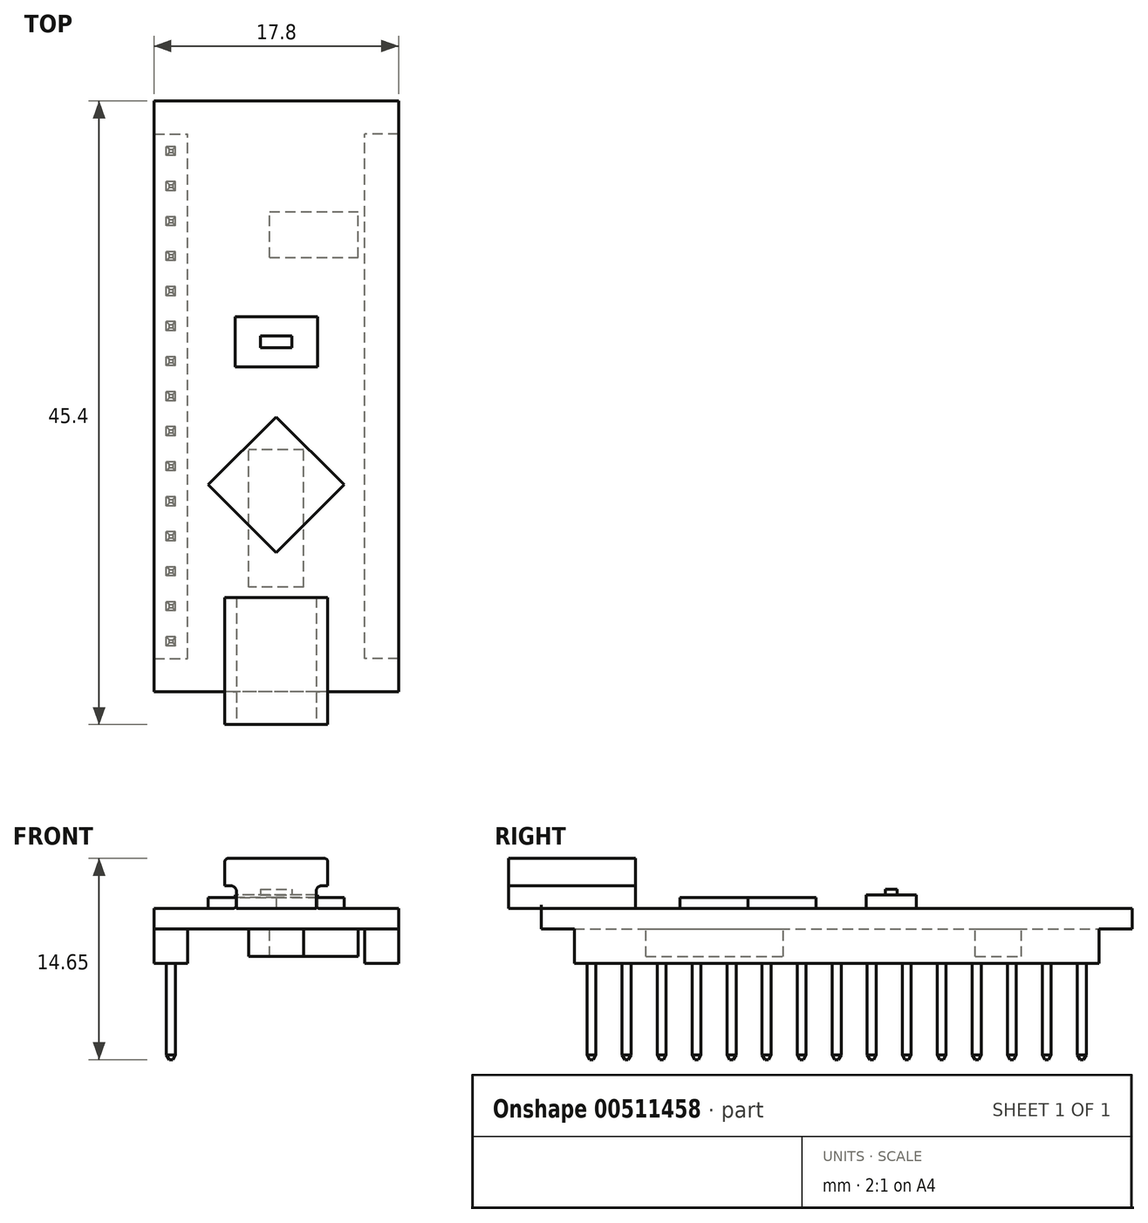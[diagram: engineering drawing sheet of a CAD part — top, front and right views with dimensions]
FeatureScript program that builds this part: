
annotation { "Feature Type Name" : "Feature", "Feature Type Description" : "" }
export const myFeature = defineFeature(function(context is Context, id is Id, definition is map)
    precondition{}
    {
        {
            var Q0;
            Q0=qCreatedBy(makeId("Top.planeOp"),FACE);
            var sketch = newSketch(context, id + "F0", { "sketchPlane" : qUnion([Q0])});
            skLineSegment(sketch, "E0.bottom", {"start": v(8.9, 21.5) * mm, "end": v(-8.9, 21.5) * mm});
            skLineSegment(sketch, "E0.top", {"start": v(8.9, -21.5) * mm, "end": v(-8.9, -21.5) * mm});
            skLineSegment(sketch, "E0.left", {"start": v(8.9, 21.5) * mm, "end": v(8.9, -21.5) * mm});
            skLineSegment(sketch, "E0.right", {"start": v(-8.9, 21.5) * mm, "end": v(-8.9, -21.5) * mm});
            skPoint(sketch, "E0.middle", {"position": v(0, 0) * mm});
            skSolve(sketch);
        }
        {
            var Q0;
            Q0=qSketchRegion(id+"F0",true);
            extrude(context, id + "F1", {"entities" : qUnion([Q0]), "depth" : 1.5 * mm, "offsetDistance" : 25 * mm});
        }
        {
            var Q0;
            Q0=makeQuery(id+"F1.opExtrude","CAP_FACE",FACE,{"disambiguationData":[OSD([sQuery(id+"F0.wireOp",EDGE,"E0.bottom"),sQuery(id+"F0.wireOp",EDGE,"E0.top"),sQuery(id+"F0.wireOp",EDGE,"E0.left"),sQuery(id+"F0.wireOp",EDGE,"E0.right")])],"isStart":false});
            var sketch = newSketch(context, id + "F2", { "sketchPlane" : qUnion([Q0])});
            skLineSegment(sketch, "E1", {"start": v(0, -1.5) * mm, "end": v(4.95, -6.45) * mm});
            skLineSegment(sketch, "E2", {"start": v(4.95, -6.45) * mm, "end": v(0, -11.4) * mm});
            skLineSegment(sketch, "E3", {"start": v(0, -11.4) * mm, "end": v(-4.95, -6.45) * mm});
            skLineSegment(sketch, "E4", {"start": v(-4.95, -6.45) * mm, "end": v(0, -1.5) * mm});
            skSolve(sketch);
        }
        {
            var Q0;
            Q0=qSketchRegion(id+"F2",true);
            extrude(context, id + "F3", {"entities" : qUnion([Q0]), "operationType" : NewBodyOperationType.ADD, "depth" : 0.8 * mm, "offsetDistance" : 25 * mm});
        }
        {
            var Q0;
            Q0=makeQuery(id+"F1.opExtrude","CAP_FACE",FACE,{"disambiguationData":[OSD([sQuery(id+"F0.wireOp",EDGE,"E0.bottom"),sQuery(id+"F0.wireOp",EDGE,"E0.top"),sQuery(id+"F0.wireOp",EDGE,"E0.left"),sQuery(id+"F0.wireOp",EDGE,"E0.right")])],"isStart":false});
            var sketch = newSketch(context, id + "F4", { "sketchPlane" : qUnion([Q0])});
            skLineSegment(sketch, "E5.bottom", {"start": v(3, 5.8) * mm, "end": v(-3, 5.8) * mm});
            skLineSegment(sketch, "E5.top", {"start": v(3, 2.15) * mm, "end": v(-3, 2.15) * mm});
            skLineSegment(sketch, "E5.left", {"start": v(3, 5.8) * mm, "end": v(3, 2.15) * mm});
            skLineSegment(sketch, "E5.right", {"start": v(-3, 5.8) * mm, "end": v(-3, 2.15) * mm});
            skPoint(sketch, "E5.middle", {"position": v(0, 3.98) * mm});
            skSolve(sketch);
        }
        {
            var Q0;
            Q0=qSketchRegion(id+"F4",true);
            extrude(context, id + "F5", {"entities" : qUnion([Q0]), "operationType" : NewBodyOperationType.ADD, "depth" : 1 * mm, "offsetDistance" : 25 * mm});
        }
        {
            var Q0;
            Q0=makeQuery(id+"F5.opExtrude","CAP_FACE",FACE,{"disambiguationData":[OSD([sQuery(id+"F4.wireOp",EDGE,"E5.bottom"),sQuery(id+"F4.wireOp",EDGE,"E5.top"),sQuery(id+"F4.wireOp",EDGE,"E5.left"),sQuery(id+"F4.wireOp",EDGE,"E5.right")])],"isStart":false});
            var sketch = newSketch(context, id + "F6", { "sketchPlane" : qUnion([Q0])});
            skLineSegment(sketch, "E6.bottom", {"start": v(-1.15, 4.4) * mm, "end": v(1.15, 4.4) * mm});
            skLineSegment(sketch, "E6.top", {"start": v(-1.15, 3.55) * mm, "end": v(1.15, 3.55) * mm});
            skLineSegment(sketch, "E6.left", {"start": v(-1.15, 4.4) * mm, "end": v(-1.15, 3.55) * mm});
            skLineSegment(sketch, "E6.right", {"start": v(1.15, 4.4) * mm, "end": v(1.15, 3.55) * mm});
            skPoint(sketch, "E6.middle", {"position": v(0, 3.98) * mm});
            skPoint(sketch, "E6.middle.positionSnap0", {"position": v(-3, 3.98) * mm});
            skPoint(sketch, "E6.middle.positionSnap1", {"position": v(0, 5.8) * mm});
            skPoint(sketch, "E6.centerSnap0", {"position": v(-3, 3.98) * mm});
            skPoint(sketch, "E6.centerSnap1", {"position": v(0, 5.8) * mm});
            skSolve(sketch);
        }
        {
            var Q0;
            Q0=qSketchRegion(id+"F6",true);
            extrude(context, id + "F7", {"entities" : qUnion([Q0]), "operationType" : NewBodyOperationType.ADD, "depth" : 0.4 * mm, "offsetDistance" : 25 * mm});
        }
        {
            var Q0;
            Q0=makeQuery(id+"F1.opExtrude","CAP_FACE",FACE,{"disambiguationData":[OSD([sQuery(id+"F0.wireOp",EDGE,"E0.bottom"),sQuery(id+"F0.wireOp",EDGE,"E0.top"),sQuery(id+"F0.wireOp",EDGE,"E0.left"),sQuery(id+"F0.wireOp",EDGE,"E0.right")])],"isStart":false});
            var sketch = newSketch(context, id + "F8", { "sketchPlane" : qUnion([Q0])});
            skLineSegment(sketch, "E7.bottom", {"start": v(3.75, -19.1) * mm, "end": v(-3.75, -19.1) * mm});
            skLineSegment(sketch, "E7.top", {"start": v(3.75, -23.9) * mm, "end": v(-3.75, -23.9) * mm});
            skLineSegment(sketch, "E7.left", {"start": v(3.75, -19.1) * mm, "end": v(3.75, -23.9) * mm});
            skLineSegment(sketch, "E7.right", {"start": v(-3.75, -19.1) * mm, "end": v(-3.75, -23.9) * mm});
            skPoint(sketch, "E7.middle", {"position": v(0, -21.5) * mm});
            skLineSegment(sketch, "E8.bottom", {"start": v(-3.75, -19.1) * mm, "end": v(3.75, -19.1) * mm});
            skLineSegment(sketch, "E8.top", {"start": v(-3.75, -14.65) * mm, "end": v(3.75, -14.65) * mm});
            skLineSegment(sketch, "E8.left", {"start": v(-3.75, -19.1) * mm, "end": v(-3.75, -14.65) * mm});
            skLineSegment(sketch, "E8.right", {"start": v(3.75, -19.1) * mm, "end": v(3.75, -14.65) * mm});
            skSolve(sketch);
        }
        {
            var Q0;
            Q0=qSketchRegion(id+"F8",true);
            extrude(context, id + "F9", {"entities" : qUnion([Q0]), "operationType" : NewBodyOperationType.ADD, "depth" : 3.65 * mm, "offsetDistance" : 25 * mm});
        }
        {
            var Q0;
            Q0=makeQuery(id+"F9.opExtrude","SWEPT_FACE",FACE,{"disambiguationData":[OSD([sQuery(id+"F8.wireOp",EDGE,"E7.top")])]});
            var sketch = newSketch(context, id + "F10", { "sketchPlane" : qUnion([Q0])});
            skLineSegment(sketch, "E9.bottom", {"start": v(-3.75, 3.15) * mm, "end": v(-2.9, 3.15) * mm});
            skLineSegment(sketch, "E9.top", {"start": v(-3.75, 1.5) * mm, "end": v(-2.9, 1.5) * mm});
            skLineSegment(sketch, "E9.left", {"start": v(-3.75, 3.15) * mm, "end": v(-3.75, 1.5) * mm});
            skLineSegment(sketch, "E9.right", {"start": v(-2.9, 3.15) * mm, "end": v(-2.9, 1.5) * mm});
            skLineSegment(sketch, "E10.bottom", {"start": v(3.75, 3.15) * mm, "end": v(2.9, 3.15) * mm});
            skLineSegment(sketch, "E10.top", {"start": v(3.75, 1.5) * mm, "end": v(2.9, 1.5) * mm});
            skLineSegment(sketch, "E10.left", {"start": v(3.75, 3.15) * mm, "end": v(3.75, 1.5) * mm});
            skLineSegment(sketch, "E10.right", {"start": v(2.9, 3.15) * mm, "end": v(2.9, 1.5) * mm});
            skSolve(sketch);
        }
        {
            var Q0;
            Q0=qSketchRegion(id+"F10",true);
            var Q1;
            Q1=makeQuery(id+"F9.opExtrude","SWEPT_FACE",FACE,{"disambiguationData":[OSD([sQuery(id+"F8.wireOp",EDGE,"E8.top")])]});
            extrude(context, id + "F11", {"entities" : qUnion([Q0]), "operationType" : NewBodyOperationType.REMOVE, "endBound" : BoundingType.UP_TO_SURFACE, "oppositeDirection" : true, "depth" : 25 * mm, "endBoundEntityFace" : qUnion([Q1]), "offsetDistance" : 25 * mm});
        }
        {
            var Q0;
            Q0=makeQuery(id+"F11.boolean.opBoolean","COPY",EDGE,{"derivedFrom":makeQuery(id+"F11.opExtrude","SWEPT_EDGE",EDGE,{"disambiguationData":[OSD([sQuery(id+"F10.wireOp",EDGE,"E9.bottom"),sQuery(id+"F10.wireOp",EDGE,"E9.right")])]})});
            var Q1;
            Q1=makeQuery(id+"F11.boolean.opBoolean","COPY",EDGE,{"derivedFrom":makeQuery(id+"F11.opExtrude","SWEPT_EDGE",EDGE,{"disambiguationData":[OSD([sQuery(id+"F8.wireOp",EDGE,"E7.top"),sQuery(id+"F8.wireOp",EDGE,"E7.right"),sQuery(id+"F10.wireOp",EDGE,"E9.bottom"),sQuery(id+"F10.wireOp",EDGE,"E9.left")])]})});
            var Q2;
            Q2=makeQuery(id+"F11.boolean.opBoolean","COPY",EDGE,{"derivedFrom":makeQuery(id+"F11.opExtrude","SWEPT_EDGE",EDGE,{"disambiguationData":[OSD([sQuery(id+"F10.wireOp",EDGE,"E10.bottom"),sQuery(id+"F10.wireOp",EDGE,"E10.right")])]})});
            var Q3;
            Q3=makeQuery(id+"F11.boolean.opBoolean","COPY",EDGE,{"derivedFrom":makeQuery(id+"F11.opExtrude","SWEPT_EDGE",EDGE,{"disambiguationData":[OSD([sQuery(id+"F8.wireOp",EDGE,"E7.top"),sQuery(id+"F8.wireOp",EDGE,"E7.left"),sQuery(id+"F10.wireOp",EDGE,"E10.bottom"),sQuery(id+"F10.wireOp",EDGE,"E10.left")])]})});
            fillet(context, id + "F12", {"entities" : qUnion([Q0, Q1, Q2, Q3]), "radius" : 0.4 * mm, "tangentPropagation" : true, "allowEdgeOverflow" : false});
        }
        {
            var Q0;
            Q0=makeQuery(id+"F9.opExtrude","CAP_EDGE",EDGE,{"disambiguationData":[OSD([sQuery(id+"F8.wireOp",EDGE,"E7.right"),sQuery(id+"F8.wireOp",EDGE,"E8.left")])],"isStart":false});
            var Q1;
            Q1=makeQuery(id+"F9.opExtrude","CAP_EDGE",EDGE,{"disambiguationData":[OSD([sQuery(id+"F8.wireOp",EDGE,"E7.left"),sQuery(id+"F8.wireOp",EDGE,"E8.right")])],"isStart":false});
            var Q2;
            {var subQ0=sQuery(id+"F8.wireOp",EDGE,"E7.top");var subQ1=sQuery(id+"F10.wireOp",EDGE,"E9.right");Q2=makeQuery(id+"F11.boolean.opBoolean","COPY",EDGE,{"disambiguationData":[topologyDisambiguationEdgeConnected([makeQuery(id+"F9.opExtrude","CAP_FACE",FACE,{"disambiguationData":[OSD([subQ0,sQuery(id+"F8.wireOp",EDGE,"E7.left"),sQuery(id+"F8.wireOp",EDGE,"E7.right"),sQuery(id+"F8.wireOp",EDGE,"E8.top"),sQuery(id+"F8.wireOp",EDGE,"E8.left"),sQuery(id+"F8.wireOp",EDGE,"E8.right")])],"isStart":true})])],"derivedFrom":makeQuery(id+"F11.opExtrude","SWEPT_EDGE",EDGE,{"disambiguationData":[OSD([subQ0,sQuery(id+"F10.wireOp",EDGE,"E9.top"),subQ1])]})});}
            var Q3;
            {var subQ0=sQuery(id+"F8.wireOp",EDGE,"E7.top");var subQ1=sQuery(id+"F10.wireOp",EDGE,"E10.right");Q3=makeQuery(id+"F11.boolean.opBoolean","COPY",EDGE,{"disambiguationData":[topologyDisambiguationEdgeConnected([makeQuery(id+"F9.opExtrude","CAP_FACE",FACE,{"disambiguationData":[OSD([subQ0,sQuery(id+"F8.wireOp",EDGE,"E7.left"),sQuery(id+"F8.wireOp",EDGE,"E7.right"),sQuery(id+"F8.wireOp",EDGE,"E8.top"),sQuery(id+"F8.wireOp",EDGE,"E8.left"),sQuery(id+"F8.wireOp",EDGE,"E8.right")])],"isStart":true})])],"derivedFrom":makeQuery(id+"F11.opExtrude","SWEPT_EDGE",EDGE,{"disambiguationData":[OSD([subQ0,sQuery(id+"F10.wireOp",EDGE,"E10.top"),subQ1])]})});}
            fillet(context, id + "F13", {"entities" : qUnion([Q0, Q1, Q2, Q3]), "radius" : 0.25 * mm, "tangentPropagation" : true, "allowEdgeOverflow" : false});
        }
        {
            var Q0;
            Q0=makeQuery(id+"F1.opExtrude","CAP_FACE",FACE,{"disambiguationData":[OSD([sQuery(id+"F0.wireOp",EDGE,"E0.bottom"),sQuery(id+"F0.wireOp",EDGE,"E0.top"),sQuery(id+"F0.wireOp",EDGE,"E0.left"),sQuery(id+"F0.wireOp",EDGE,"E0.right")])],"isStart":true});
            var sketch = newSketch(context, id + "F14", { "sketchPlane" : qUnion([Q0])});
            skLineSegment(sketch, "E11.bottom", {"start": v(-8.9, 19.1) * mm, "end": v(-6.45, 19.1) * mm});
            skLineSegment(sketch, "E11.top", {"start": v(-8.9, -19.1) * mm, "end": v(-6.45, -19.1) * mm});
            skLineSegment(sketch, "E11.left", {"start": v(-8.9, 19.1) * mm, "end": v(-8.9, -19.1) * mm});
            skLineSegment(sketch, "E11.right", {"start": v(-6.45, 19.1) * mm, "end": v(-6.45, -19.1) * mm});
            skLineSegment(sketch, "E12.bottom", {"start": v(8.9, 19.1) * mm, "end": v(6.45, 19.1) * mm});
            skLineSegment(sketch, "E12.top", {"start": v(8.9, -19.1) * mm, "end": v(6.45, -19.1) * mm});
            skLineSegment(sketch, "E12.left", {"start": v(8.9, 19.1) * mm, "end": v(8.9, -19.1) * mm});
            skLineSegment(sketch, "E12.right", {"start": v(6.45, 19.1) * mm, "end": v(6.45, -19.1) * mm});
            skSolve(sketch);
        }
        {
            var Q0;
            Q0=qSketchRegion(id+"F14",true);
            extrude(context, id + "F15", {"entities" : qUnion([Q0]), "operationType" : NewBodyOperationType.ADD, "depth" : 2.5 * mm, "offsetDistance" : 25 * mm});
        }
        {
            var Q0;
            Q0=makeQuery(id+"F15.opExtrude","CAP_FACE",FACE,{"disambiguationData":[OSD([sQuery(id+"F14.wireOp",EDGE,"E11.bottom"),sQuery(id+"F14.wireOp",EDGE,"E11.top"),sQuery(id+"F14.wireOp",EDGE,"E11.left"),sQuery(id+"F14.wireOp",EDGE,"E11.right")])],"isStart":false});
            var sketch = newSketch(context, id + "F16", { "sketchPlane" : qUnion([Q0])});
            skLineSegment(sketch, "E13.bottom", {"start": v(-7.35, 18.18) * mm, "end": v(-8, 18.18) * mm});
            skLineSegment(sketch, "E13.top", {"start": v(-7.35, 17.53) * mm, "end": v(-8, 17.53) * mm});
            skLineSegment(sketch, "E13.left", {"start": v(-7.35, 18.18) * mm, "end": v(-7.35, 17.53) * mm});
            skLineSegment(sketch, "E13.right", {"start": v(-8, 18.18) * mm, "end": v(-8, 17.53) * mm});
            skPoint(sketch, "E13.middle", {"position": v(-7.68, 17.85) * mm});
            skPoint(sketch, "E13.middle.positionSnap0", {"position": v(-7.68, 19.1) * mm});
            skPoint(sketch, "E13.centerSnap0", {"position": v(-7.68, 19.1) * mm});
            skLineSegment(sketch, "E14.0.1.0", {"start": v(-7.35, 15.63) * mm, "end": v(-8, 15.63) * mm});
            skLineSegment(sketch, "E14.0.1.1", {"start": v(-7.35, 15.63) * mm, "end": v(-7.35, 14.98) * mm});
            skLineSegment(sketch, "E14.0.1.2", {"start": v(-8, 15.63) * mm, "end": v(-8, 14.98) * mm});
            skLineSegment(sketch, "E14.0.1.3", {"start": v(-7.35, 14.98) * mm, "end": v(-8, 14.98) * mm});
            skLineSegment(sketch, "E14.0.2.0", {"start": v(-7.35, 13.08) * mm, "end": v(-8, 13.08) * mm});
            skLineSegment(sketch, "E14.0.2.1", {"start": v(-7.35, 13.08) * mm, "end": v(-7.35, 12.43) * mm});
            skLineSegment(sketch, "E14.0.2.2", {"start": v(-8, 13.08) * mm, "end": v(-8, 12.43) * mm});
            skLineSegment(sketch, "E14.0.2.3", {"start": v(-7.35, 12.43) * mm, "end": v(-8, 12.43) * mm});
            skLineSegment(sketch, "E14.0.3.0", {"start": v(-7.35, 10.53) * mm, "end": v(-8, 10.53) * mm});
            skLineSegment(sketch, "E14.0.3.1", {"start": v(-7.35, 10.53) * mm, "end": v(-7.35, 9.88) * mm});
            skLineSegment(sketch, "E14.0.3.2", {"start": v(-8, 10.53) * mm, "end": v(-8, 9.88) * mm});
            skLineSegment(sketch, "E14.0.3.3", {"start": v(-7.35, 9.88) * mm, "end": v(-8, 9.88) * mm});
            skLineSegment(sketch, "E14.0.4.0", {"start": v(-7.35, 7.98) * mm, "end": v(-8, 7.98) * mm});
            skLineSegment(sketch, "E14.0.4.1", {"start": v(-7.35, 7.98) * mm, "end": v(-7.35, 7.33) * mm});
            skLineSegment(sketch, "E14.0.4.2", {"start": v(-8, 7.98) * mm, "end": v(-8, 7.33) * mm});
            skLineSegment(sketch, "E14.0.4.3", {"start": v(-7.35, 7.33) * mm, "end": v(-8, 7.33) * mm});
            skLineSegment(sketch, "E14.0.5.0", {"start": v(-7.35, 5.43) * mm, "end": v(-8, 5.43) * mm});
            skLineSegment(sketch, "E14.0.5.1", {"start": v(-7.35, 5.43) * mm, "end": v(-7.35, 4.78) * mm});
            skLineSegment(sketch, "E14.0.5.2", {"start": v(-8, 5.43) * mm, "end": v(-8, 4.78) * mm});
            skLineSegment(sketch, "E14.0.5.3", {"start": v(-7.35, 4.78) * mm, "end": v(-8, 4.78) * mm});
            skLineSegment(sketch, "E14.0.6.0", {"start": v(-7.35, 2.88) * mm, "end": v(-8, 2.88) * mm});
            skLineSegment(sketch, "E14.0.6.1", {"start": v(-7.35, 2.88) * mm, "end": v(-7.35, 2.23) * mm});
            skLineSegment(sketch, "E14.0.6.2", {"start": v(-8, 2.88) * mm, "end": v(-8, 2.23) * mm});
            skLineSegment(sketch, "E14.0.6.3", {"start": v(-7.35, 2.23) * mm, "end": v(-8, 2.23) * mm});
            skLineSegment(sketch, "E14.0.7.0", {"start": v(-7.35, 0.33) * mm, "end": v(-8, 0.33) * mm});
            skLineSegment(sketch, "E14.0.7.1", {"start": v(-7.35, 0.33) * mm, "end": v(-7.35, -0.32) * mm});
            skLineSegment(sketch, "E14.0.7.2", {"start": v(-8, 0.33) * mm, "end": v(-8, -0.32) * mm});
            skLineSegment(sketch, "E14.0.7.3", {"start": v(-7.35, -0.32) * mm, "end": v(-8, -0.32) * mm});
            skLineSegment(sketch, "E14.0.8.0", {"start": v(-7.35, -2.22) * mm, "end": v(-8, -2.22) * mm});
            skLineSegment(sketch, "E14.0.8.1", {"start": v(-7.35, -2.22) * mm, "end": v(-7.35, -2.87) * mm});
            skLineSegment(sketch, "E14.0.8.2", {"start": v(-8, -2.22) * mm, "end": v(-8, -2.87) * mm});
            skLineSegment(sketch, "E14.0.8.3", {"start": v(-7.35, -2.87) * mm, "end": v(-8, -2.87) * mm});
            skLineSegment(sketch, "E14.0.9.0", {"start": v(-7.35, -4.77) * mm, "end": v(-8, -4.77) * mm});
            skLineSegment(sketch, "E14.0.9.1", {"start": v(-7.35, -4.77) * mm, "end": v(-7.35, -5.42) * mm});
            skLineSegment(sketch, "E14.0.9.2", {"start": v(-8, -4.77) * mm, "end": v(-8, -5.42) * mm});
            skLineSegment(sketch, "E14.0.9.3", {"start": v(-7.35, -5.42) * mm, "end": v(-8, -5.42) * mm});
            skLineSegment(sketch, "E14.0.10.0", {"start": v(-7.35, -7.32) * mm, "end": v(-8, -7.32) * mm});
            skLineSegment(sketch, "E14.0.10.1", {"start": v(-7.35, -7.32) * mm, "end": v(-7.35, -7.97) * mm});
            skLineSegment(sketch, "E14.0.10.2", {"start": v(-8, -7.32) * mm, "end": v(-8, -7.97) * mm});
            skLineSegment(sketch, "E14.0.10.3", {"start": v(-7.35, -7.97) * mm, "end": v(-8, -7.97) * mm});
            skLineSegment(sketch, "E14.0.11.0", {"start": v(-7.35, -9.87) * mm, "end": v(-8, -9.87) * mm});
            skLineSegment(sketch, "E14.0.11.1", {"start": v(-7.35, -9.87) * mm, "end": v(-7.35, -10.52) * mm});
            skLineSegment(sketch, "E14.0.11.2", {"start": v(-8, -9.87) * mm, "end": v(-8, -10.52) * mm});
            skLineSegment(sketch, "E14.0.11.3", {"start": v(-7.35, -10.52) * mm, "end": v(-8, -10.52) * mm});
            skLineSegment(sketch, "E14.0.12.0", {"start": v(-7.35, -12.42) * mm, "end": v(-8, -12.42) * mm});
            skLineSegment(sketch, "E14.0.12.1", {"start": v(-7.35, -12.42) * mm, "end": v(-7.35, -13.07) * mm});
            skLineSegment(sketch, "E14.0.12.2", {"start": v(-8, -12.42) * mm, "end": v(-8, -13.07) * mm});
            skLineSegment(sketch, "E14.0.12.3", {"start": v(-7.35, -13.07) * mm, "end": v(-8, -13.07) * mm});
            skLineSegment(sketch, "E14.0.13.0", {"start": v(-7.35, -14.97) * mm, "end": v(-8, -14.97) * mm});
            skLineSegment(sketch, "E14.0.13.1", {"start": v(-7.35, -14.97) * mm, "end": v(-7.35, -15.62) * mm});
            skLineSegment(sketch, "E14.0.13.2", {"start": v(-8, -14.97) * mm, "end": v(-8, -15.62) * mm});
            skLineSegment(sketch, "E14.0.13.3", {"start": v(-7.35, -15.62) * mm, "end": v(-8, -15.62) * mm});
            skLineSegment(sketch, "E14.0.14.0", {"start": v(-7.35, -17.52) * mm, "end": v(-8, -17.52) * mm});
            skLineSegment(sketch, "E14.0.14.1", {"start": v(-7.35, -17.52) * mm, "end": v(-7.35, -18.17) * mm});
            skLineSegment(sketch, "E14.0.14.2", {"start": v(-8, -17.52) * mm, "end": v(-8, -18.17) * mm});
            skLineSegment(sketch, "E14.0.14.3", {"start": v(-7.35, -18.17) * mm, "end": v(-8, -18.17) * mm});
            skLineSegment(sketch, "E14.direction1", {"start": v(-8, 18.18) * mm, "end": v(17, 18.18) * mm, "construction": true});
            skLineSegment(sketch, "E14.direction2", {"start": v(-8, 18.18) * mm, "end": v(-8, 15.63) * mm, "construction": true});
            skSolve(sketch);
        }
        {
            var Q0;
            Q0=qSketchRegion(id+"F16",true);
            extrude(context, id + "F17", {"entities" : qUnion([Q0]), "operationType" : NewBodyOperationType.ADD, "depth" : 7 * mm, "offsetDistance" : 25 * mm});
        }
        {
            var Q0;
            Q0=makeQuery(id+"F1.opExtrude","CAP_EDGE",EDGE,{"disambiguationData":[OSD([sQuery(id+"F0.wireOp",EDGE,"E0.top")])],"isStart":true});
            cPoint(context, id + "F18", {"entities" : qUnion([Q0]), "parameter" : 0.5});
        }
        {
            var Q0;
            Q0=makeQuery(id+"F1.opExtrude","CAP_EDGE",EDGE,{"disambiguationData":[OSD([sQuery(id+"F0.wireOp",EDGE,"E0.bottom")])],"isStart":true});
            cPoint(context, id + "F19", {"entities" : qUnion([Q0]), "parameter" : 0.5});
        }
        {
            var Q0;
            Q0=makeQuery(id+"F1.opExtrude","CAP_EDGE",EDGE,{"disambiguationData":[OSD([sQuery(id+"F0.wireOp",EDGE,"E0.bottom")])],"isStart":false});
            cPoint(context, id + "F20", {"entities" : qUnion([Q0]), "parameter" : 0.5});
        }
        {
            var Q0;
            Q0=qCreatedBy(id+"F18",VERTEX);
            var Q1;
            Q1=qCreatedBy(id+"F19",VERTEX);
            var Q2;
            Q2=qCreatedBy(id+"F20",VERTEX);
            cPlane(context, id + "F21", {"entities" : qUnion([Q0, Q1, Q2]), "cplaneType" : CPlaneType.THREE_POINT, "offset" : 25 * mm, "width" : 150 * mm, "height" : 150 * mm});
        }
        {
            var Q0;
            Q0=makeQuery(id+"F17.opExtrude","CAP_EDGE",EDGE,{"disambiguationData":[OSD([sQuery(id+"F16.wireOp",EDGE,"E13.right")])],"isStart":false});
            var Q1;
            Q1=makeQuery(id+"F17.opExtrude","CAP_EDGE",EDGE,{"disambiguationData":[OSD([sQuery(id+"F16.wireOp",EDGE,"E13.top")])],"isStart":false});
            var Q2;
            Q2=makeQuery(id+"F17.opExtrude","CAP_EDGE",EDGE,{"disambiguationData":[OSD([sQuery(id+"F16.wireOp",EDGE,"E13.left")])],"isStart":false});
            var Q3;
            Q3=makeQuery(id+"F17.opExtrude","CAP_EDGE",EDGE,{"disambiguationData":[OSD([sQuery(id+"F16.wireOp",EDGE,"E13.bottom")])],"isStart":false});
            var Q4;
            Q4=makeQuery(id+"F17.opExtrude","CAP_EDGE",EDGE,{"disambiguationData":[OSD([sQuery(id+"F16.wireOp",EDGE,"E14.0.2.2")])],"isStart":false});
            var Q5;
            Q5=makeQuery(id+"F17.opExtrude","CAP_EDGE",EDGE,{"disambiguationData":[OSD([sQuery(id+"F16.wireOp",EDGE,"E14.0.2.0")])],"isStart":false});
            var Q6;
            Q6=makeQuery(id+"F17.opExtrude","CAP_EDGE",EDGE,{"disambiguationData":[OSD([sQuery(id+"F16.wireOp",EDGE,"E14.0.1.2")])],"isStart":false});
            var Q7;
            Q7=makeQuery(id+"F17.opExtrude","CAP_EDGE",EDGE,{"disambiguationData":[OSD([sQuery(id+"F16.wireOp",EDGE,"E14.0.1.0")])],"isStart":false});
            var Q8;
            Q8=makeQuery(id+"F17.opExtrude","CAP_EDGE",EDGE,{"disambiguationData":[OSD([sQuery(id+"F16.wireOp",EDGE,"E14.0.3.2")])],"isStart":false});
            var Q9;
            Q9=makeQuery(id+"F17.opExtrude","CAP_EDGE",EDGE,{"disambiguationData":[OSD([sQuery(id+"F16.wireOp",EDGE,"E14.0.3.0")])],"isStart":false});
            var Q10;
            Q10=makeQuery(id+"F17.opExtrude","CAP_EDGE",EDGE,{"disambiguationData":[OSD([sQuery(id+"F16.wireOp",EDGE,"E14.0.4.2")])],"isStart":false});
            var Q11;
            Q11=makeQuery(id+"F17.opExtrude","CAP_EDGE",EDGE,{"disambiguationData":[OSD([sQuery(id+"F16.wireOp",EDGE,"E14.0.4.0")])],"isStart":false});
            var Q12;
            Q12=makeQuery(id+"F17.opExtrude","CAP_EDGE",EDGE,{"disambiguationData":[OSD([sQuery(id+"F16.wireOp",EDGE,"E14.0.5.2")])],"isStart":false});
            var Q13;
            Q13=makeQuery(id+"F17.opExtrude","CAP_EDGE",EDGE,{"disambiguationData":[OSD([sQuery(id+"F16.wireOp",EDGE,"E14.0.5.0")])],"isStart":false});
            var Q14;
            Q14=makeQuery(id+"F17.opExtrude","CAP_EDGE",EDGE,{"disambiguationData":[OSD([sQuery(id+"F16.wireOp",EDGE,"E14.0.6.2")])],"isStart":false});
            var Q15;
            Q15=makeQuery(id+"F17.opExtrude","CAP_EDGE",EDGE,{"disambiguationData":[OSD([sQuery(id+"F16.wireOp",EDGE,"E14.0.6.0")])],"isStart":false});
            var Q16;
            Q16=makeQuery(id+"F17.opExtrude","CAP_EDGE",EDGE,{"disambiguationData":[OSD([sQuery(id+"F16.wireOp",EDGE,"E14.0.7.2")])],"isStart":false});
            var Q17;
            Q17=makeQuery(id+"F17.opExtrude","CAP_EDGE",EDGE,{"disambiguationData":[OSD([sQuery(id+"F16.wireOp",EDGE,"E14.0.7.0")])],"isStart":false});
            var Q18;
            Q18=makeQuery(id+"F17.opExtrude","CAP_EDGE",EDGE,{"disambiguationData":[OSD([sQuery(id+"F16.wireOp",EDGE,"E14.0.8.2")])],"isStart":false});
            var Q19;
            Q19=makeQuery(id+"F17.opExtrude","CAP_EDGE",EDGE,{"disambiguationData":[OSD([sQuery(id+"F16.wireOp",EDGE,"E14.0.8.0")])],"isStart":false});
            var Q20;
            Q20=makeQuery(id+"F17.opExtrude","CAP_EDGE",EDGE,{"disambiguationData":[OSD([sQuery(id+"F16.wireOp",EDGE,"E14.0.9.2")])],"isStart":false});
            var Q21;
            Q21=makeQuery(id+"F17.opExtrude","CAP_EDGE",EDGE,{"disambiguationData":[OSD([sQuery(id+"F16.wireOp",EDGE,"E14.0.9.0")])],"isStart":false});
            var Q22;
            Q22=makeQuery(id+"F17.opExtrude","CAP_EDGE",EDGE,{"disambiguationData":[OSD([sQuery(id+"F16.wireOp",EDGE,"E14.0.10.2")])],"isStart":false});
            var Q23;
            Q23=makeQuery(id+"F17.opExtrude","CAP_EDGE",EDGE,{"disambiguationData":[OSD([sQuery(id+"F16.wireOp",EDGE,"E14.0.10.0")])],"isStart":false});
            var Q24;
            Q24=makeQuery(id+"F17.opExtrude","CAP_EDGE",EDGE,{"disambiguationData":[OSD([sQuery(id+"F16.wireOp",EDGE,"E14.0.11.2")])],"isStart":false});
            var Q25;
            Q25=makeQuery(id+"F17.opExtrude","CAP_EDGE",EDGE,{"disambiguationData":[OSD([sQuery(id+"F16.wireOp",EDGE,"E14.0.11.0")])],"isStart":false});
            var Q26;
            Q26=makeQuery(id+"F17.opExtrude","CAP_EDGE",EDGE,{"disambiguationData":[OSD([sQuery(id+"F16.wireOp",EDGE,"E14.0.12.2")])],"isStart":false});
            var Q27;
            Q27=makeQuery(id+"F17.opExtrude","CAP_EDGE",EDGE,{"disambiguationData":[OSD([sQuery(id+"F16.wireOp",EDGE,"E14.0.12.0")])],"isStart":false});
            var Q28;
            Q28=makeQuery(id+"F17.opExtrude","CAP_EDGE",EDGE,{"disambiguationData":[OSD([sQuery(id+"F16.wireOp",EDGE,"E14.0.13.2")])],"isStart":false});
            var Q29;
            Q29=makeQuery(id+"F17.opExtrude","CAP_EDGE",EDGE,{"disambiguationData":[OSD([sQuery(id+"F16.wireOp",EDGE,"E14.0.13.0")])],"isStart":false});
            var Q30;
            Q30=makeQuery(id+"F17.opExtrude","CAP_EDGE",EDGE,{"disambiguationData":[OSD([sQuery(id+"F16.wireOp",EDGE,"E14.0.14.2")])],"isStart":false});
            var Q31;
            Q31=makeQuery(id+"F17.opExtrude","CAP_EDGE",EDGE,{"disambiguationData":[OSD([sQuery(id+"F16.wireOp",EDGE,"E14.0.14.0")])],"isStart":false});
            chamfer(context, id + "F22", {"entities" : qUnion([Q0, Q1, Q2, Q3, Q4, Q5, Q6, Q7, Q8, Q9, Q10, Q11, Q12, Q13, Q14, Q15, Q16, Q17, Q18, Q19, Q20, Q21, Q22, Q23, Q24, Q25, Q26, Q27, Q28, Q29, Q30, Q31]), "chamferType" : ChamferType.OFFSET_ANGLE, "width" : 0.2 * mm, "oppositeDirection" : false, "angle" : 60 * degree, "tangentPropagation" : true});
        }
        {
            var Q0;
            Q0=makeQuery(id+"F17.opExtrude","CAP_EDGE",EDGE,{"disambiguationData":[OSD([sQuery(id+"F16.wireOp",EDGE,"E14.0.1.1")])],"isStart":false});
            var Q1;
            Q1=makeQuery(id+"F17.opExtrude","CAP_EDGE",EDGE,{"disambiguationData":[OSD([sQuery(id+"F16.wireOp",EDGE,"E14.0.1.3")])],"isStart":false});
            var Q2;
            Q2=makeQuery(id+"F17.opExtrude","CAP_EDGE",EDGE,{"disambiguationData":[OSD([sQuery(id+"F16.wireOp",EDGE,"E14.0.2.1")])],"isStart":false});
            var Q3;
            Q3=makeQuery(id+"F17.opExtrude","CAP_EDGE",EDGE,{"disambiguationData":[OSD([sQuery(id+"F16.wireOp",EDGE,"E14.0.2.3")])],"isStart":false});
            var Q4;
            Q4=makeQuery(id+"F17.opExtrude","CAP_EDGE",EDGE,{"disambiguationData":[OSD([sQuery(id+"F16.wireOp",EDGE,"E14.0.3.1")])],"isStart":false});
            var Q5;
            Q5=makeQuery(id+"F17.opExtrude","CAP_EDGE",EDGE,{"disambiguationData":[OSD([sQuery(id+"F16.wireOp",EDGE,"E14.0.3.3")])],"isStart":false});
            var Q6;
            Q6=makeQuery(id+"F17.opExtrude","CAP_EDGE",EDGE,{"disambiguationData":[OSD([sQuery(id+"F16.wireOp",EDGE,"E14.0.4.1")])],"isStart":false});
            var Q7;
            Q7=makeQuery(id+"F17.opExtrude","CAP_EDGE",EDGE,{"disambiguationData":[OSD([sQuery(id+"F16.wireOp",EDGE,"E14.0.4.3")])],"isStart":false});
            var Q8;
            Q8=makeQuery(id+"F17.opExtrude","CAP_EDGE",EDGE,{"disambiguationData":[OSD([sQuery(id+"F16.wireOp",EDGE,"E14.0.5.1")])],"isStart":false});
            var Q9;
            Q9=makeQuery(id+"F17.opExtrude","CAP_EDGE",EDGE,{"disambiguationData":[OSD([sQuery(id+"F16.wireOp",EDGE,"E14.0.5.3")])],"isStart":false});
            var Q10;
            Q10=makeQuery(id+"F17.opExtrude","CAP_EDGE",EDGE,{"disambiguationData":[OSD([sQuery(id+"F16.wireOp",EDGE,"E14.0.6.1")])],"isStart":false});
            var Q11;
            Q11=makeQuery(id+"F17.opExtrude","CAP_EDGE",EDGE,{"disambiguationData":[OSD([sQuery(id+"F16.wireOp",EDGE,"E14.0.6.3")])],"isStart":false});
            var Q12;
            Q12=makeQuery(id+"F17.opExtrude","CAP_EDGE",EDGE,{"disambiguationData":[OSD([sQuery(id+"F16.wireOp",EDGE,"E14.0.7.1")])],"isStart":false});
            var Q13;
            Q13=makeQuery(id+"F17.opExtrude","CAP_EDGE",EDGE,{"disambiguationData":[OSD([sQuery(id+"F16.wireOp",EDGE,"E14.0.7.3")])],"isStart":false});
            var Q14;
            Q14=makeQuery(id+"F17.opExtrude","CAP_EDGE",EDGE,{"disambiguationData":[OSD([sQuery(id+"F16.wireOp",EDGE,"E14.0.8.1")])],"isStart":false});
            var Q15;
            Q15=makeQuery(id+"F17.opExtrude","CAP_EDGE",EDGE,{"disambiguationData":[OSD([sQuery(id+"F16.wireOp",EDGE,"E14.0.8.3")])],"isStart":false});
            var Q16;
            Q16=makeQuery(id+"F17.opExtrude","CAP_EDGE",EDGE,{"disambiguationData":[OSD([sQuery(id+"F16.wireOp",EDGE,"E14.0.9.1")])],"isStart":false});
            var Q17;
            Q17=makeQuery(id+"F17.opExtrude","CAP_EDGE",EDGE,{"disambiguationData":[OSD([sQuery(id+"F16.wireOp",EDGE,"E14.0.9.3")])],"isStart":false});
            var Q18;
            Q18=makeQuery(id+"F17.opExtrude","CAP_EDGE",EDGE,{"disambiguationData":[OSD([sQuery(id+"F16.wireOp",EDGE,"E14.0.10.1")])],"isStart":false});
            var Q19;
            Q19=makeQuery(id+"F17.opExtrude","CAP_EDGE",EDGE,{"disambiguationData":[OSD([sQuery(id+"F16.wireOp",EDGE,"E14.0.10.3")])],"isStart":false});
            var Q20;
            Q20=makeQuery(id+"F17.opExtrude","CAP_EDGE",EDGE,{"disambiguationData":[OSD([sQuery(id+"F16.wireOp",EDGE,"E14.0.11.1")])],"isStart":false});
            var Q21;
            Q21=makeQuery(id+"F17.opExtrude","CAP_EDGE",EDGE,{"disambiguationData":[OSD([sQuery(id+"F16.wireOp",EDGE,"E14.0.11.3")])],"isStart":false});
            var Q22;
            Q22=makeQuery(id+"F17.opExtrude","CAP_EDGE",EDGE,{"disambiguationData":[OSD([sQuery(id+"F16.wireOp",EDGE,"E14.0.12.1")])],"isStart":false});
            var Q23;
            Q23=makeQuery(id+"F17.opExtrude","CAP_EDGE",EDGE,{"disambiguationData":[OSD([sQuery(id+"F16.wireOp",EDGE,"E14.0.12.3")])],"isStart":false});
            var Q24;
            Q24=makeQuery(id+"F17.opExtrude","CAP_EDGE",EDGE,{"disambiguationData":[OSD([sQuery(id+"F16.wireOp",EDGE,"E14.0.13.1")])],"isStart":false});
            var Q25;
            Q25=makeQuery(id+"F17.opExtrude","CAP_EDGE",EDGE,{"disambiguationData":[OSD([sQuery(id+"F16.wireOp",EDGE,"E14.0.13.3")])],"isStart":false});
            var Q26;
            Q26=makeQuery(id+"F17.opExtrude","CAP_EDGE",EDGE,{"disambiguationData":[OSD([sQuery(id+"F16.wireOp",EDGE,"E14.0.14.1")])],"isStart":false});
            var Q27;
            Q27=makeQuery(id+"F17.opExtrude","CAP_EDGE",EDGE,{"disambiguationData":[OSD([sQuery(id+"F16.wireOp",EDGE,"E14.0.14.3")])],"isStart":false});
            chamfer(context, id + "F23", {"entities" : qUnion([Q0, Q1, Q2, Q3, Q4, Q5, Q6, Q7, Q8, Q9, Q10, Q11, Q12, Q13, Q14, Q15, Q16, Q17, Q18, Q19, Q20, Q21, Q22, Q23, Q24, Q25, Q26, Q27]), "chamferType" : ChamferType.OFFSET_ANGLE, "width" : 0.2 * mm, "oppositeDirection" : true, "angle" : 60 * degree, "tangentPropagation" : true});
        }
        {
            var Q0;
            Q0=makeQuery(id+"F1.opExtrude","CAP_FACE",FACE,{"disambiguationData":[OSD([sQuery(id+"F0.wireOp",EDGE,"E0.bottom"),sQuery(id+"F0.wireOp",EDGE,"E0.top"),sQuery(id+"F0.wireOp",EDGE,"E0.left"),sQuery(id+"F0.wireOp",EDGE,"E0.right")])],"isStart":true});
            var sketch = newSketch(context, id + "F24", { "sketchPlane" : qUnion([Q0])});
            skLineSegment(sketch, "E15.bottom", {"start": v(2, 13.9) * mm, "end": v(-2, 13.9) * mm});
            skLineSegment(sketch, "E15.top", {"start": v(2, 3.9) * mm, "end": v(-2, 3.9) * mm});
            skLineSegment(sketch, "E15.left", {"start": v(2, 13.9) * mm, "end": v(2, 3.9) * mm});
            skLineSegment(sketch, "E15.right", {"start": v(-2, 13.9) * mm, "end": v(-2, 3.9) * mm});
            skPoint(sketch, "E15.middle", {"position": v(0, 8.9) * mm});
            skPoint(sketch, "E15.middle.positionSnap0", {"position": v(0, 21.5) * mm});
            skPoint(sketch, "E15.centerSnap0", {"position": v(0, 21.5) * mm});
            skSolve(sketch);
        }
        {
            var Q0;
            Q0=qSketchRegion(id+"F24",true);
            extrude(context, id + "F25", {"entities" : qUnion([Q0]), "operationType" : NewBodyOperationType.ADD, "depth" : 2 * mm, "offsetDistance" : 25 * mm});
        }
        {
            var Q0;
            Q0=makeQuery(id+"F1.opExtrude","CAP_FACE",FACE,{"disambiguationData":[OSD([sQuery(id+"F0.wireOp",EDGE,"E0.bottom"),sQuery(id+"F0.wireOp",EDGE,"E0.top"),sQuery(id+"F0.wireOp",EDGE,"E0.left"),sQuery(id+"F0.wireOp",EDGE,"E0.right")])],"isStart":true});
            var sketch = newSketch(context, id + "F26", { "sketchPlane" : qUnion([Q0])});
            skLineSegment(sketch, "E16.bottom", {"start": v(-0.5, -10.1) * mm, "end": v(5.95, -10.1) * mm});
            skLineSegment(sketch, "E16.top", {"start": v(-0.5, -13.45) * mm, "end": v(5.95, -13.45) * mm});
            skLineSegment(sketch, "E16.left", {"start": v(-0.5, -10.1) * mm, "end": v(-0.5, -13.45) * mm});
            skLineSegment(sketch, "E16.right", {"start": v(5.95, -10.1) * mm, "end": v(5.95, -13.45) * mm});
            skSolve(sketch);
        }
        {
            var Q0;
            Q0=makeQuery(id+"F26.imprint","IMPRINT",FACE,{"disambiguationData":[TD([[makeQuery(id+"F26.imprint","IMPRINT",EDGE,{"derivedFrom":sQuery(id+"F26.wireOp",EDGE,"E16.bottom")}),-1.0]])]});
            extrude(context, id + "F27", {"entities" : qUnion([Q0]), "operationType" : NewBodyOperationType.ADD, "depth" : 2 * mm, "offsetDistance" : 25 * mm});
        }
    });
